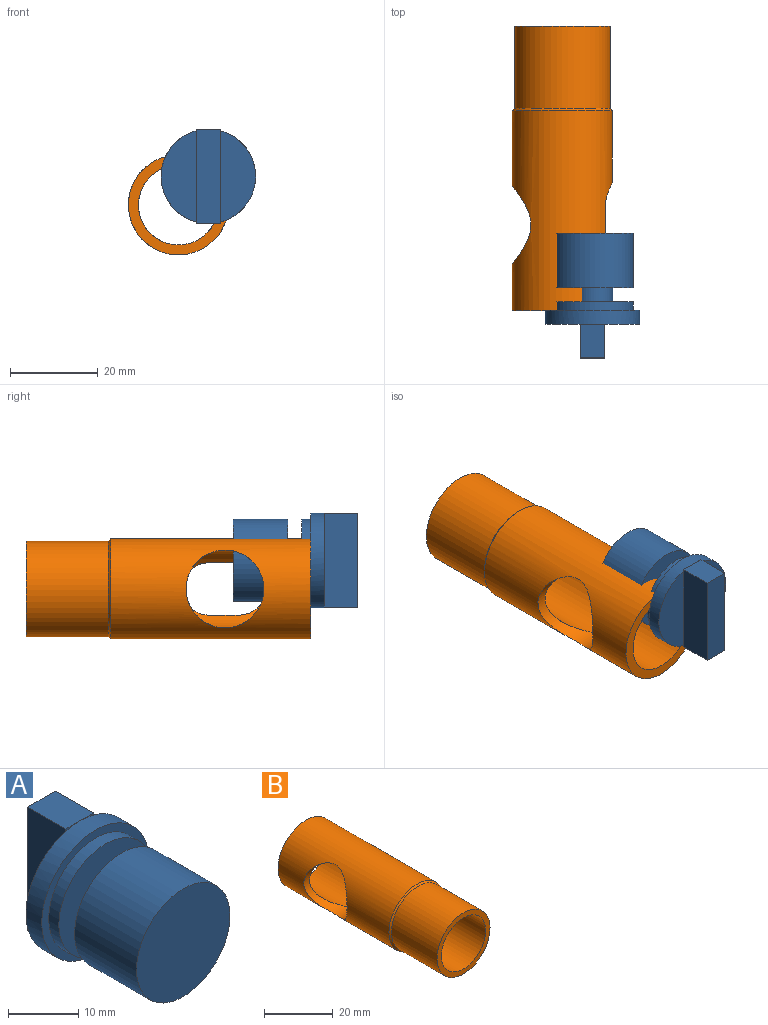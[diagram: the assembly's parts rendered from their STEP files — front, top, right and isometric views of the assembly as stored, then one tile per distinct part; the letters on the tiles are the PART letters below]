
ASSEMBLY  parts=2 mates=1
PART A: 19 faces, bbox 21.6x28.5x21.6 mm
  f0: plane 20.85x8mm, normal (0,1,0), area 123.4mm2, adj f2,f18
  f1: plane 20.85x8mm, normal (0,1,0), area 123.4mm2, adj f2,f17
  f2: cylinder r=10.79mm len=21.59mm, axis (0,1,0), area 215.4mm2, adj f0,f1,f3,f10,f11,f12,f13,f14
  f3: plane 21.59x21.59mm, normal (0,-1,0), area 88.6mm2, adj f2,f4
  f4: cylinder r=9.4mm len=18.8mm, axis (0,1,0), area 120mm2, adj f3,f5
  f5: plane 18.8x18.8mm, normal (0,-1,0), area 208.1mm2, adj f4,f6
  f6: cylinder r=4.7mm len=9.4mm, axis (0,1,0), area 93.7mm2, adj f5,f7
  f7: plane 18.8x18.8mm, normal (0,1,0), area 208.1mm2, adj f6,f8
  f8: cylinder r=9.4mm len=18.8mm, axis (0,1,0), area 734.9mm2, adj f7,f9
  f9: plane 18.8x18.8mm, normal (0,-1,0), area 277.5mm2, adj f8
  f10: plane 2.74x0.37mm, normal (0,-1,0), area 0.3mm2, adj f2,f14,f17
  f11: plane 2.74x0.37mm, normal (0,-1,0), area 0.3mm2, adj f2,f14,f18
  f12: plane 2.79x0.37mm, normal (0,-1,0), area 0.3mm2, adj f2,f16,f17
  f13: plane 2.79x0.37mm, normal (0,-1,0), area 0.3mm2, adj f2,f16,f18
  f14: plane 7.66x5.59mm, normal (0,0,-1), area 42.8mm2, adj f2,f10,f11,f15,f17,f18
  f15: plane 21.59x5.59mm, normal (0,1,0), area 120.6mm2, adj f14,f16,f17,f18
  f16: plane 7.66x5.59mm, normal (0,0,1), area 42.8mm2, adj f12,f13,f15,f17,f18
  f17: plane 21.59x7.66mm, normal (1,0,0), area 165.4mm2, adj f1,f10,f12,f14,f15,f16
  f18: plane 21.59x7.66mm, normal (-1,0,0), area 165.4mm2, adj f0,f11,f13,f14,f15,f16
PART B: 11 faces, bbox 22.9x65x22.9 mm
  f0: plane 21.84x21.84mm, normal (0,-1,0), area 112.1mm2, adj f1,f5
  f1: cylinder r=9.14mm len=65.02mm, axis (0,-1,0), area 3220.6mm2, adj f0,f2,f6,f7,f8,f9,f10
  f2: plane 22.86x22.86mm, normal (0,1,0), area 147.8mm2, adj f1,f3
  f3: cylinder r=11.43mm len=45.72mm, axis (0,-1,0), area 2804.6mm2, adj f2,f4,f6,f7,f8,f9,f10
  f4: cone r=10.92mm half-angle=45deg, axis (0,1,0), area 50.4mm2, adj f3,f5
  f5: cylinder r=10.92mm len=21.84mm, axis (0,-1,0), area 1289.9mm2, adj f0,f4
  f6: cylinder r=8.89mm len=17.78mm, axis (1,0,0), area 180.6mm2, adj f1,f3
  f7: plane 7.11x2.82mm, normal (0,0,1), area 20.1mm2, adj f1,f3,f8,f10
  f8: cylinder r=5.97mm len=11.94mm, axis (-1,0,0), area 47.5mm2, adj f1,f3,f7,f9
  f9: plane 7.11x2.82mm, normal (0,0,-1), area 20.1mm2, adj f1,f3,f8,f10
  f10: cylinder r=5.97mm len=11.93mm, axis (-1,0,0), area 47.4mm2, adj f1,f3,f7,f9
PLACE A rot(axis=(1,0,0),180deg) t=(6.85,-62.99,6.54)mm
PLACE B rot(axis=(1,0,0),180deg) t=(0,1.1,0)mm
MATE planar A.f2 <-> B.f1  axis (0,1,0) through (6.85,-65.02,6.54)mm
